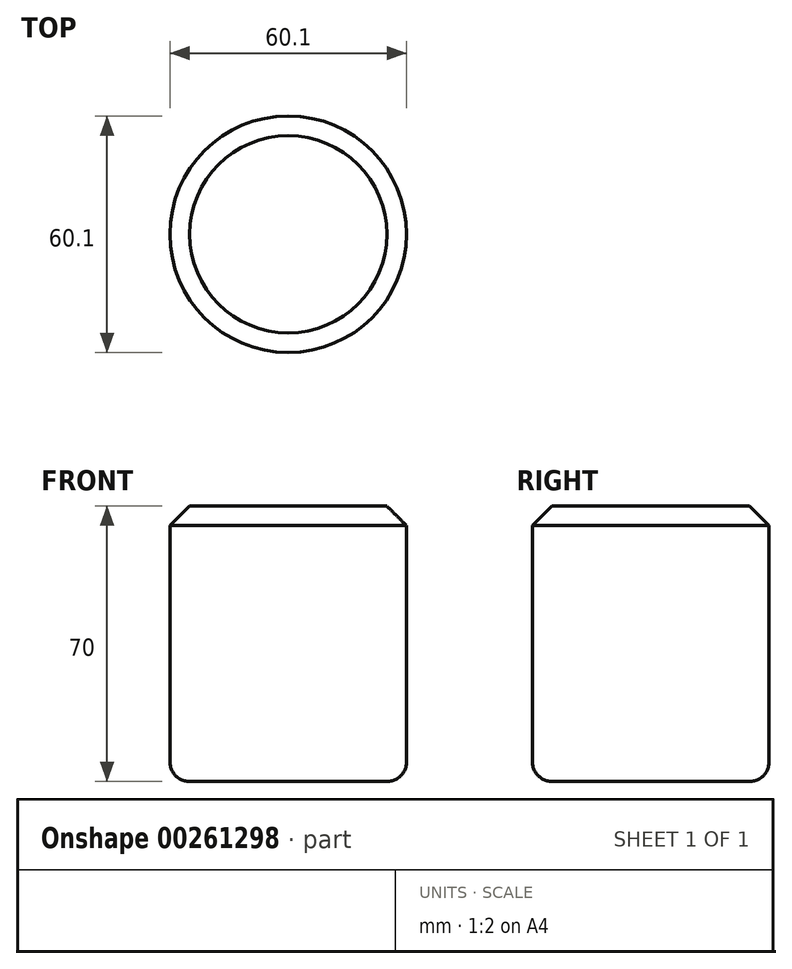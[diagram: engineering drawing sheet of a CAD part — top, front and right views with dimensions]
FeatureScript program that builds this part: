
annotation { "Feature Type Name" : "Feature", "Feature Type Description" : "" }
export const myFeature = defineFeature(function(context is Context, id is Id, definition is map)
    precondition{}
    {
        {
            var Q0;
            Q0=qCreatedBy(makeId("Top.planeOp"),FACE);
            var sketch = newSketch(context, id + "F0", { "sketchPlane" : qUnion([Q0])});
            skCircle(sketch, "E0", {"center": v(0, 0) * mm, "radius": 30.05 * mm});
            skSolve(sketch);
        }
        {
            var Q0;
            Q0=makeQuery(id+"F0.imprint","IMPRINT",FACE,{"disambiguationData":[TD([[makeQuery(id+"F0.imprint","IMPRINT",EDGE,{"derivedFrom":sQuery(id+"F0.wireOp",EDGE,"E0")}),1.0]])]});
            extrude(context, id + "F1", {"entities" : qUnion([Q0]), "depth" : 70 * mm});
        }
        {
            var Q0;
            Q0=makeQuery(id+"F1.opExtrude","CAP_EDGE",EDGE,{"disambiguationData":[OSD([sQuery(id+"F0.wireOp",EDGE,"E0")])],"isStart":false});
            chamfer(context, id + "F2", {"entities" : qUnion([Q0]), "width" : 5 * mm, "tangentPropagation" : true});
        }
        {
            var Q0;
            Q0=makeQuery(id+"F1.opExtrude","CAP_FACE",FACE,{"disambiguationData":[OSD([sQuery(id+"F0.wireOp",EDGE,"E0")])],"isStart":true});
            fillet(context, id + "F3", {"entities" : qUnion([Q0]), "radius" : 5 * mm, "tangentPropagation" : true, "allowEdgeOverflow" : false});
        }
    });
